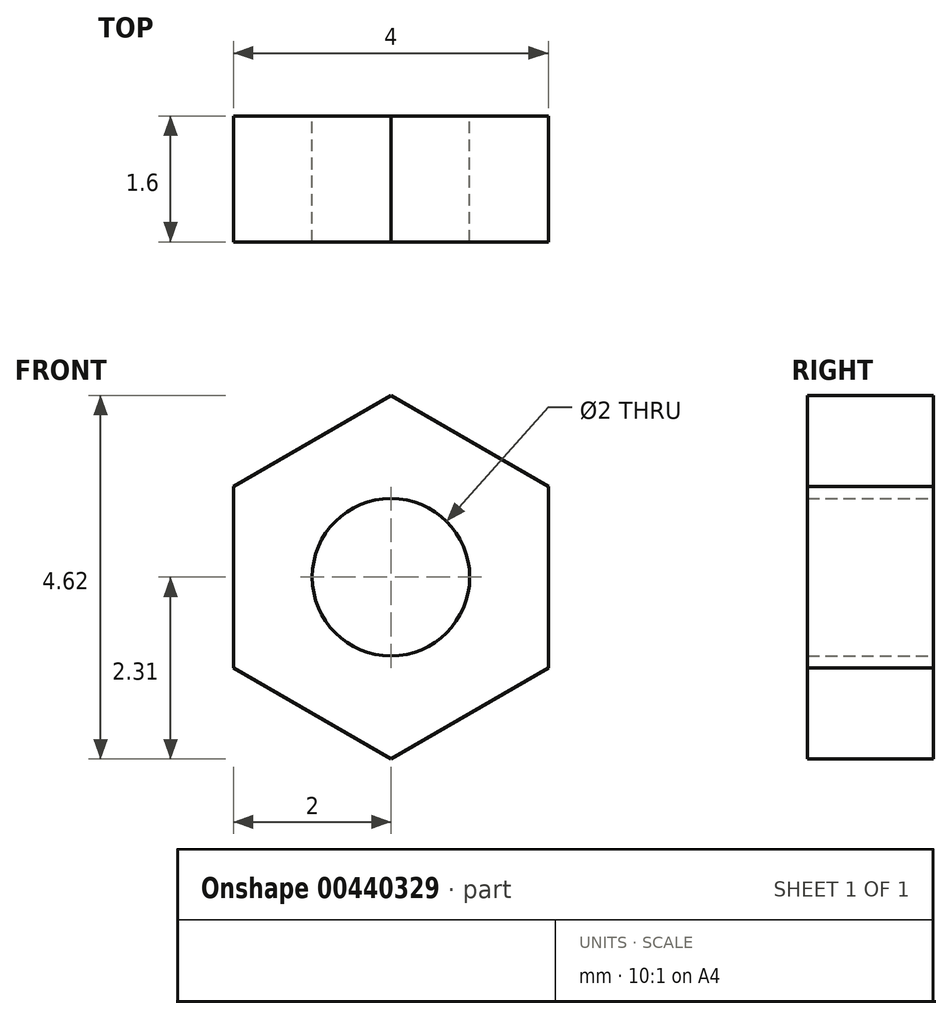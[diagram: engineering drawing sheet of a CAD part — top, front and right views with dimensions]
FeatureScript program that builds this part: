
annotation { "Feature Type Name" : "Feature", "Feature Type Description" : "" }
export const myFeature = defineFeature(function(context is Context, id is Id, definition is map)
    precondition{}
    {
        {
            var Q0;
            Q0=qCreatedBy(makeId("Front.planeOp"),FACE);
            var sketch = newSketch(context, id + "F0", { "sketchPlane" : qUnion([Q0])});
            skCircle(sketch, "E0", {"center": v(0, 0) * mm, "radius": 1 * mm});
            skCircle(sketch, "E1.cCircle", {"center": v(0, 0) * mm, "radius": 2.3 * mm, "construction": true});
            skLineSegment(sketch, "E1.0", {"start": v(0, 2.3) * mm, "end": v(2, 1.15) * mm});
            skLineSegment(sketch, "E1.1", {"start": v(2, 1.15) * mm, "end": v(2, -1.15) * mm});
            skLineSegment(sketch, "E1.2", {"start": v(2, -1.15) * mm, "end": v(0, -2.3) * mm});
            skLineSegment(sketch, "E1.3", {"start": v(0, -2.3) * mm, "end": v(-2, -1.15) * mm});
            skLineSegment(sketch, "E1.4", {"start": v(-2, -1.15) * mm, "end": v(-2, 1.15) * mm});
            skLineSegment(sketch, "E1.5", {"start": v(-2, 1.15) * mm, "end": v(0, 2.3) * mm});
            skSolve(sketch);
        }
        {
            var Q0;
            Q0=makeQuery(id+"F0.imprint","IMPRINT",FACE,{"disambiguationData":[TD([[makeQuery(id+"F0.imprint","IMPRINT",EDGE,{"derivedFrom":sQuery(id+"F0.wireOp",EDGE,"E0")}),-1.0]])]});
            extrude(context, id + "F1", {"entities" : qUnion([Q0]), "depth" : 1.6 * mm});
        }
    });
